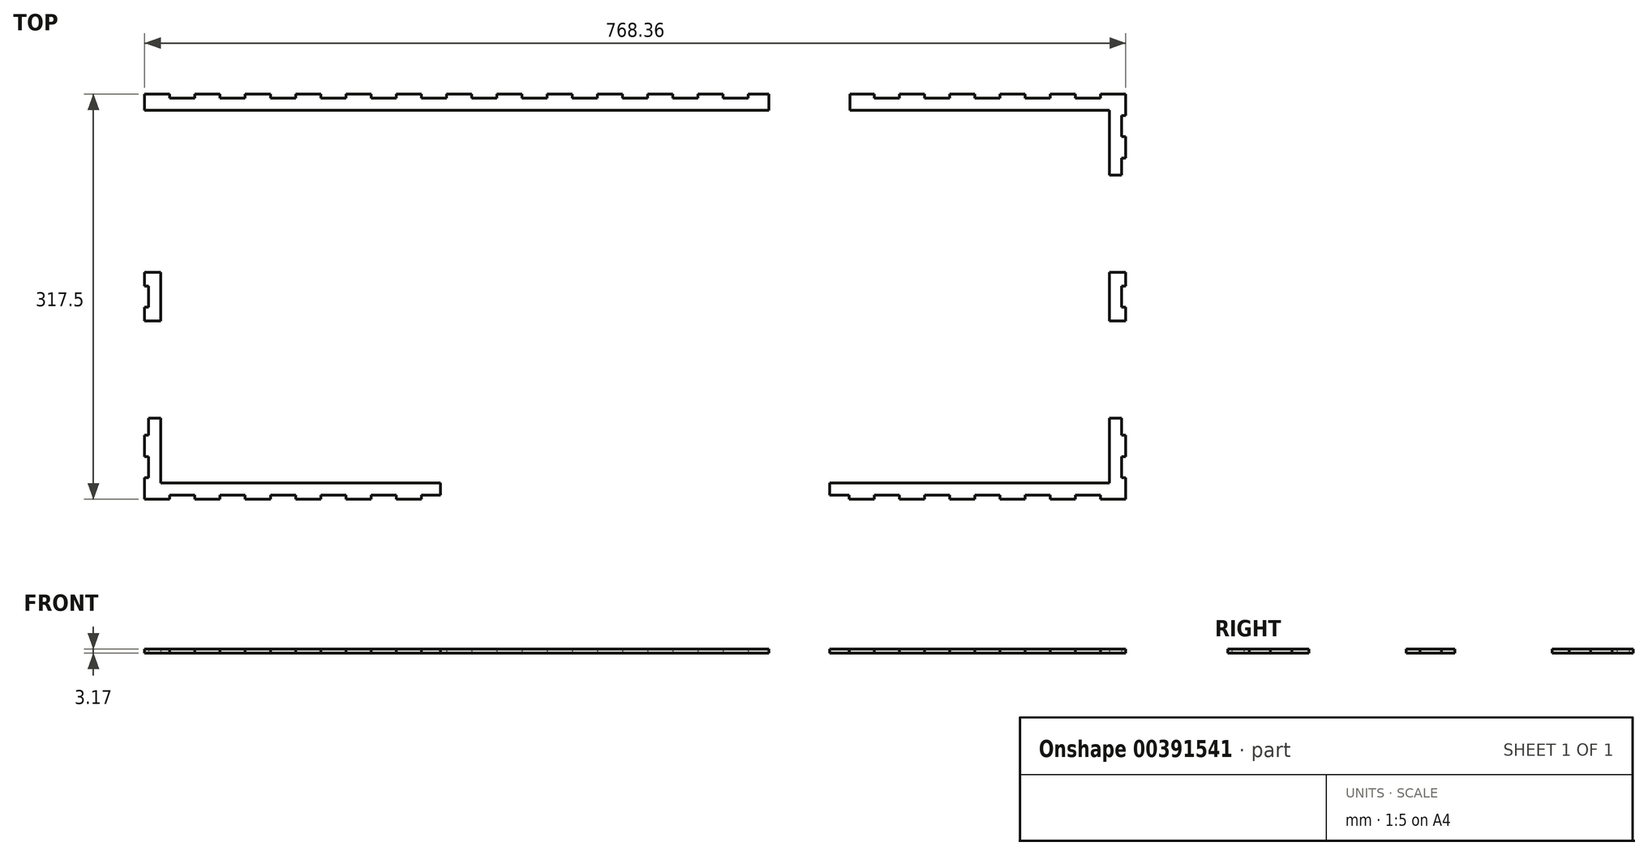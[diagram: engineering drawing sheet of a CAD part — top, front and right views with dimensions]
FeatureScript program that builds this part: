
annotation { "Feature Type Name" : "Feature", "Feature Type Description" : "" }
export const myFeature = defineFeature(function(context is Context, id is Id, definition is map)
    precondition{}
    {
        {
            var Q0;
            Q0=qCreatedBy(makeId("Top.planeOp"),FACE);
            var sketch = newSketch(context, id + "F0", { "sketchPlane" : qUnion([Q0])});
            skLineSegment(sketch, "E0.right", {"start": v(-384.18, -158.75) * mm, "end": v(-384.18, 158.75) * mm, "construction": true});
            skPoint(sketch, "E0.middle", {"position": v(0, 0) * mm});
            skLineSegment(sketch, "E1.bottom", {"start": v(-384.18, 158.75) * mm, "end": v(-364.47, 158.75) * mm});
            skLineSegment(sketch, "E1.left", {"start": v(-384.18, 158.75) * mm, "end": v(-384.18, 142.04) * mm});
            skLineSegment(sketch, "E2.right", {"start": v(-381, 142.04) * mm, "end": v(-381, 125.33) * mm});
            skLineSegment(sketch, "E3", {"start": v(-384.18, 142.04) * mm, "end": v(-381, 142.04) * mm});
            skLineSegment(sketch, "E4", {"start": v(-364.47, 158.75) * mm, "end": v(-364.47, 155.57) * mm});
            skLineSegment(sketch, "E5", {"start": v(-364.47, 155.57) * mm, "end": v(-344.77, 155.57) * mm});
            skLineSegment(sketch, "E6", {"start": v(384.18, 158.75) * mm, "end": v(-384.18, 158.75) * mm, "construction": true});
            skLineSegment(sketch, "E7", {"start": v(-381, 125.33) * mm, "end": v(-384.18, 125.33) * mm});
            skLineSegment(sketch, "E8.1.0.1", {"start": v(-384.18, 108.62) * mm, "end": v(-381, 108.62) * mm});
            skLineSegment(sketch, "E8.1.0.3", {"start": v(-384.17, 125.33) * mm, "end": v(-384.18, 108.62) * mm});
            skLineSegment(sketch, "E8.4.0.0", {"start": v(-381, -8.36) * mm, "end": v(-384.17, -8.36) * mm});
            skLineSegment(sketch, "E8.4.0.1", {"start": v(-384.17, 8.36) * mm, "end": v(-381, 8.36) * mm});
            skLineSegment(sketch, "E8.4.0.2", {"start": v(-381, 8.36) * mm, "end": v(-381, -8.36) * mm});
            skLineSegment(sketch, "E8.7.0.0", {"start": v(-381, -108.62) * mm, "end": v(-384.17, -108.62) * mm});
            skLineSegment(sketch, "E8.8.0.0", {"start": v(-381, -142.04) * mm, "end": v(-384.17, -142.04) * mm});
            skLineSegment(sketch, "E8.8.0.1", {"start": v(-384.17, -125.33) * mm, "end": v(-381, -125.33) * mm});
            skLineSegment(sketch, "E8.8.0.2", {"start": v(-381, -125.33) * mm, "end": v(-381, -142.04) * mm});
            skLineSegment(sketch, "E8.8.0.3", {"start": v(-384.17, -108.62) * mm, "end": v(-384.17, -125.33) * mm});
            skLineSegment(sketch, "E8.9.0.1", {"start": v(-384.17, -158.75) * mm, "end": v(-381, -158.75) * mm});
            skLineSegment(sketch, "E8.9.0.3", {"start": v(-384.17, -142.04) * mm, "end": v(-384.17, -158.75) * mm});
            skLineSegment(sketch, "E8.direction1", {"start": v(-384.18, 125.33) * mm, "end": v(-384.18, 91.9) * mm, "construction": true});
            skLineSegment(sketch, "E9", {"start": v(-344.77, 155.57) * mm, "end": v(-344.77, 158.75) * mm});
            skLineSegment(sketch, "E10.1.0.0", {"start": v(-325.07, 158.75) * mm, "end": v(-325.07, 155.58) * mm});
            skLineSegment(sketch, "E10.1.0.1", {"start": v(-325.07, 155.58) * mm, "end": v(-305.37, 155.58) * mm});
            skLineSegment(sketch, "E10.1.0.2", {"start": v(-305.37, 155.58) * mm, "end": v(-305.37, 158.75) * mm});
            skLineSegment(sketch, "E10.1.0.3", {"start": v(-344.77, 158.75) * mm, "end": v(-325.07, 158.75) * mm});
            skLineSegment(sketch, "E10.2.0.0", {"start": v(-285.67, 158.75) * mm, "end": v(-285.67, 155.58) * mm});
            skLineSegment(sketch, "E10.2.0.1", {"start": v(-285.67, 155.58) * mm, "end": v(-265.97, 155.58) * mm});
            skLineSegment(sketch, "E10.2.0.2", {"start": v(-265.97, 155.58) * mm, "end": v(-265.97, 158.75) * mm});
            skLineSegment(sketch, "E10.2.0.3", {"start": v(-305.37, 158.75) * mm, "end": v(-285.67, 158.75) * mm});
            skLineSegment(sketch, "E10.3.0.0", {"start": v(-246.27, 158.75) * mm, "end": v(-246.27, 155.58) * mm});
            skLineSegment(sketch, "E10.3.0.1", {"start": v(-246.27, 155.58) * mm, "end": v(-226.56, 155.58) * mm});
            skLineSegment(sketch, "E10.3.0.2", {"start": v(-226.56, 155.58) * mm, "end": v(-226.56, 158.75) * mm});
            skLineSegment(sketch, "E10.3.0.3", {"start": v(-265.97, 158.75) * mm, "end": v(-246.27, 158.75) * mm});
            skLineSegment(sketch, "E10.4.0.0", {"start": v(-206.86, 158.75) * mm, "end": v(-206.86, 155.58) * mm});
            skLineSegment(sketch, "E10.4.0.1", {"start": v(-206.86, 155.58) * mm, "end": v(-187.16, 155.58) * mm});
            skLineSegment(sketch, "E10.4.0.2", {"start": v(-187.16, 155.58) * mm, "end": v(-187.16, 158.75) * mm});
            skLineSegment(sketch, "E10.4.0.3", {"start": v(-226.56, 158.75) * mm, "end": v(-206.86, 158.75) * mm});
            skLineSegment(sketch, "E10.5.0.0", {"start": v(-167.46, 158.75) * mm, "end": v(-167.46, 155.58) * mm});
            skLineSegment(sketch, "E10.5.0.1", {"start": v(-167.46, 155.58) * mm, "end": v(-147.76, 155.58) * mm});
            skLineSegment(sketch, "E10.5.0.2", {"start": v(-147.76, 155.58) * mm, "end": v(-147.76, 158.75) * mm});
            skLineSegment(sketch, "E10.5.0.3", {"start": v(-187.16, 158.75) * mm, "end": v(-167.46, 158.75) * mm});
            skLineSegment(sketch, "E10.6.0.0", {"start": v(-128.06, 158.75) * mm, "end": v(-128.06, 155.58) * mm});
            skLineSegment(sketch, "E10.6.0.1", {"start": v(-128.06, 155.58) * mm, "end": v(-108.36, 155.58) * mm});
            skLineSegment(sketch, "E10.6.0.2", {"start": v(-108.36, 155.58) * mm, "end": v(-108.36, 158.75) * mm});
            skLineSegment(sketch, "E10.6.0.3", {"start": v(-147.76, 158.75) * mm, "end": v(-128.06, 158.75) * mm});
            skLineSegment(sketch, "E10.7.0.0", {"start": v(-88.66, 158.75) * mm, "end": v(-88.66, 155.58) * mm});
            skLineSegment(sketch, "E10.7.0.1", {"start": v(-88.66, 155.58) * mm, "end": v(-68.95, 155.58) * mm});
            skLineSegment(sketch, "E10.7.0.2", {"start": v(-68.95, 155.58) * mm, "end": v(-68.95, 158.75) * mm});
            skLineSegment(sketch, "E10.7.0.3", {"start": v(-108.36, 158.75) * mm, "end": v(-88.66, 158.75) * mm});
            skLineSegment(sketch, "E10.8.0.0", {"start": v(-49.25, 158.75) * mm, "end": v(-49.25, 155.58) * mm});
            skLineSegment(sketch, "E10.8.0.1", {"start": v(-49.25, 155.58) * mm, "end": v(-29.55, 155.58) * mm});
            skLineSegment(sketch, "E10.8.0.2", {"start": v(-29.55, 155.58) * mm, "end": v(-29.55, 158.75) * mm});
            skLineSegment(sketch, "E10.8.0.3", {"start": v(-68.95, 158.75) * mm, "end": v(-49.25, 158.75) * mm});
            skLineSegment(sketch, "E10.9.0.0", {"start": v(-9.85, 158.75) * mm, "end": v(-9.85, 155.58) * mm});
            skLineSegment(sketch, "E10.9.0.1", {"start": v(-9.85, 155.58) * mm, "end": v(9.85, 155.58) * mm});
            skLineSegment(sketch, "E10.9.0.2", {"start": v(9.85, 155.58) * mm, "end": v(9.85, 158.75) * mm});
            skLineSegment(sketch, "E10.9.0.3", {"start": v(-29.55, 158.75) * mm, "end": v(-9.85, 158.75) * mm});
            skLineSegment(sketch, "E10.10.0.0", {"start": v(29.55, 158.75) * mm, "end": v(29.55, 155.58) * mm});
            skLineSegment(sketch, "E10.10.0.1", {"start": v(29.55, 155.58) * mm, "end": v(49.25, 155.58) * mm});
            skLineSegment(sketch, "E10.10.0.2", {"start": v(49.25, 155.58) * mm, "end": v(49.25, 158.75) * mm});
            skLineSegment(sketch, "E10.10.0.3", {"start": v(9.85, 158.75) * mm, "end": v(29.55, 158.75) * mm});
            skLineSegment(sketch, "E10.11.0.0", {"start": v(68.95, 158.75) * mm, "end": v(68.95, 155.58) * mm});
            skLineSegment(sketch, "E10.11.0.1", {"start": v(68.95, 155.58) * mm, "end": v(88.66, 155.58) * mm});
            skLineSegment(sketch, "E10.11.0.2", {"start": v(88.66, 155.58) * mm, "end": v(88.66, 158.75) * mm});
            skLineSegment(sketch, "E10.11.0.3", {"start": v(49.25, 158.75) * mm, "end": v(68.95, 158.75) * mm});
            skLineSegment(sketch, "E10.12.0.0", {"start": v(108.36, 158.75) * mm, "end": v(108.36, 155.58) * mm});
            skLineSegment(sketch, "E10.12.0.3", {"start": v(88.66, 158.75) * mm, "end": v(108.36, 158.75) * mm});
            skLineSegment(sketch, "E10.16.0.2", {"start": v(285.67, 155.58) * mm, "end": v(285.67, 158.75) * mm});
            skLineSegment(sketch, "E10.17.0.0", {"start": v(305.37, 158.75) * mm, "end": v(305.37, 155.58) * mm});
            skLineSegment(sketch, "E10.17.0.1", {"start": v(305.37, 155.58) * mm, "end": v(325.07, 155.58) * mm});
            skLineSegment(sketch, "E10.17.0.2", {"start": v(325.07, 155.58) * mm, "end": v(325.07, 158.75) * mm});
            skLineSegment(sketch, "E10.17.0.3", {"start": v(285.67, 158.75) * mm, "end": v(305.37, 158.75) * mm});
            skLineSegment(sketch, "E10.18.0.0", {"start": v(344.77, 158.75) * mm, "end": v(344.77, 155.58) * mm});
            skLineSegment(sketch, "E10.18.0.1", {"start": v(344.77, 155.58) * mm, "end": v(364.47, 155.58) * mm});
            skLineSegment(sketch, "E10.18.0.2", {"start": v(364.47, 155.58) * mm, "end": v(364.47, 158.75) * mm});
            skLineSegment(sketch, "E10.18.0.3", {"start": v(325.07, 158.75) * mm, "end": v(344.77, 158.75) * mm});
            skLineSegment(sketch, "E10.19.0.0", {"start": v(384.18, 158.75) * mm, "end": v(384.18, 155.58) * mm});
            skLineSegment(sketch, "E10.19.0.3", {"start": v(364.47, 158.75) * mm, "end": v(384.18, 158.75) * mm});
            skLineSegment(sketch, "E10.direction1", {"start": v(-384.18, 158.75) * mm, "end": v(-344.77, 158.75) * mm, "construction": true});
            skLineSegment(sketch, "E11.MirrorCS", {"start": v(384.18, -158.75) * mm, "end": v(384.18, -155.58) * mm});
            skLineSegment(sketch, "E12.MirrorCS", {"start": v(-344.77, -155.57) * mm, "end": v(-344.77, -158.75) * mm});
            skLineSegment(sketch, "E13.MirrorCS", {"start": v(108.36, -158.75) * mm, "end": v(108.36, -155.58) * mm});
            skLineSegment(sketch, "E14.MirrorCS", {"start": v(285.67, -155.58) * mm, "end": v(285.67, -158.75) * mm});
            skLineSegment(sketch, "E15.MirrorCS", {"start": v(-285.67, -158.75) * mm, "end": v(-285.67, -155.58) * mm});
            skLineSegment(sketch, "E16.MirrorCS", {"start": v(49.25, -155.58) * mm, "end": v(49.25, -158.75) * mm});
            skLineSegment(sketch, "E17.MirrorCS", {"start": v(-108.36, -155.58) * mm, "end": v(-108.36, -158.75) * mm});
            skLineSegment(sketch, "E18.MirrorCS", {"start": v(-265.97, -155.58) * mm, "end": v(-265.97, -158.75) * mm});
            skLineSegment(sketch, "E19.MirrorCS", {"start": v(-29.55, -155.58) * mm, "end": v(-29.55, -158.75) * mm});
            skLineSegment(sketch, "E20.MirrorCS", {"start": v(364.47, -155.58) * mm, "end": v(364.47, -158.75) * mm});
            skLineSegment(sketch, "E21.MirrorCS", {"start": v(-206.86, -158.75) * mm, "end": v(-206.86, -155.58) * mm});
            skLineSegment(sketch, "E22.MirrorCS", {"start": v(-147.76, -155.58) * mm, "end": v(-147.76, -158.75) * mm});
            skLineSegment(sketch, "E23.MirrorCS", {"start": v(-305.37, -155.58) * mm, "end": v(-305.37, -158.75) * mm});
            skLineSegment(sketch, "E24.MirrorCS", {"start": v(206.86, -155.58) * mm, "end": v(206.86, -158.75) * mm});
            skLineSegment(sketch, "E25.MirrorCS", {"start": v(344.77, -158.75) * mm, "end": v(344.77, -155.58) * mm});
            skLineSegment(sketch, "E26.MirrorCS", {"start": v(128.06, -155.58) * mm, "end": v(128.06, -158.75) * mm});
            skLineSegment(sketch, "E27.MirrorCS", {"start": v(9.85, -155.58) * mm, "end": v(9.85, -158.75) * mm});
            skLineSegment(sketch, "E28.MirrorCS", {"start": v(-364.47, -158.75) * mm, "end": v(-364.47, -155.57) * mm});
            skLineSegment(sketch, "E29.MirrorCS", {"start": v(325.07, -155.58) * mm, "end": v(325.07, -158.75) * mm});
            skLineSegment(sketch, "E30.MirrorCS", {"start": v(167.46, -155.58) * mm, "end": v(167.46, -158.75) * mm});
            skLineSegment(sketch, "E31.MirrorCS", {"start": v(147.76, -158.75) * mm, "end": v(147.76, -155.58) * mm});
            skLineSegment(sketch, "E32.MirrorCS", {"start": v(305.37, -158.75) * mm, "end": v(305.37, -155.58) * mm});
            skLineSegment(sketch, "E33.MirrorCS", {"start": v(-88.66, -158.75) * mm, "end": v(-88.66, -155.58) * mm});
            skLineSegment(sketch, "E34.MirrorCS", {"start": v(29.55, -158.75) * mm, "end": v(29.55, -155.58) * mm});
            skLineSegment(sketch, "E35.MirrorCS", {"start": v(-128.06, -158.75) * mm, "end": v(-128.06, -155.58) * mm});
            skLineSegment(sketch, "E36.MirrorCS", {"start": v(-226.56, -155.58) * mm, "end": v(-226.56, -158.75) * mm});
            skLineSegment(sketch, "E37.MirrorCS", {"start": v(88.66, -155.58) * mm, "end": v(88.66, -158.75) * mm});
            skLineSegment(sketch, "E38.MirrorCS", {"start": v(246.27, -155.58) * mm, "end": v(246.27, -158.75) * mm});
            skLineSegment(sketch, "E39.MirrorCS", {"start": v(-68.95, -155.58) * mm, "end": v(-68.95, -158.75) * mm});
            skLineSegment(sketch, "E40.MirrorCS", {"start": v(265.97, -158.75) * mm, "end": v(265.97, -155.58) * mm});
            skLineSegment(sketch, "E41.MirrorCS", {"start": v(-325.07, -158.75) * mm, "end": v(-325.07, -155.58) * mm});
            skLineSegment(sketch, "E42.MirrorCS", {"start": v(187.16, -158.75) * mm, "end": v(187.16, -155.58) * mm});
            skLineSegment(sketch, "E43.MirrorCS", {"start": v(-187.16, -155.58) * mm, "end": v(-187.16, -158.75) * mm});
            skLineSegment(sketch, "E44.MirrorCS", {"start": v(-167.46, -158.75) * mm, "end": v(-167.46, -155.58) * mm});
            skLineSegment(sketch, "E45.MirrorCS", {"start": v(-9.85, -158.75) * mm, "end": v(-9.85, -155.58) * mm});
            skLineSegment(sketch, "E46.MirrorCS", {"start": v(-246.27, -158.75) * mm, "end": v(-246.27, -155.58) * mm});
            skLineSegment(sketch, "E47.MirrorCS", {"start": v(226.56, -158.75) * mm, "end": v(226.56, -155.58) * mm});
            skLineSegment(sketch, "E48.MirrorCS", {"start": v(68.95, -158.75) * mm, "end": v(68.95, -155.58) * mm});
            skLineSegment(sketch, "E49.MirrorCS", {"start": v(-49.25, -158.75) * mm, "end": v(-49.25, -155.58) * mm});
            skLineSegment(sketch, "E50.MirrorCS", {"start": v(-68.95, -158.75) * mm, "end": v(-49.25, -158.75) * mm});
            skLineSegment(sketch, "E51.MirrorCS", {"start": v(-226.56, -158.75) * mm, "end": v(-206.86, -158.75) * mm});
            skLineSegment(sketch, "E52.MirrorCS", {"start": v(246.27, -158.75) * mm, "end": v(265.97, -158.75) * mm});
            skLineSegment(sketch, "E53.MirrorCS", {"start": v(206.86, -158.75) * mm, "end": v(226.56, -158.75) * mm});
            skLineSegment(sketch, "E54.MirrorCS", {"start": v(49.25, -158.75) * mm, "end": v(68.95, -158.75) * mm});
            skLineSegment(sketch, "E55.MirrorCS", {"start": v(-265.97, -158.75) * mm, "end": v(-246.27, -158.75) * mm});
            skLineSegment(sketch, "E56.MirrorCS", {"start": v(-108.36, -158.75) * mm, "end": v(-88.66, -158.75) * mm});
            skLineSegment(sketch, "E57.MirrorCS", {"start": v(88.66, -158.75) * mm, "end": v(108.36, -158.75) * mm});
            skLineSegment(sketch, "E58.MirrorCS", {"start": v(-344.77, -158.75) * mm, "end": v(-325.07, -158.75) * mm});
            skLineSegment(sketch, "E59.MirrorCS", {"start": v(285.67, -158.75) * mm, "end": v(305.37, -158.75) * mm});
            skLineSegment(sketch, "E60.MirrorCS", {"start": v(128.06, -158.75) * mm, "end": v(147.76, -158.75) * mm});
            skLineSegment(sketch, "E61.MirrorCS", {"start": v(-384.18, -158.75) * mm, "end": v(-364.47, -158.75) * mm});
            skLineSegment(sketch, "E62.MirrorCS", {"start": v(167.46, -158.75) * mm, "end": v(187.16, -158.75) * mm});
            skLineSegment(sketch, "E63.MirrorCS", {"start": v(325.07, -158.75) * mm, "end": v(344.77, -158.75) * mm});
            skLineSegment(sketch, "E64.MirrorCS", {"start": v(364.47, -158.75) * mm, "end": v(384.18, -158.75) * mm});
            skLineSegment(sketch, "E65.MirrorCS", {"start": v(-29.55, -158.75) * mm, "end": v(-9.85, -158.75) * mm});
            skLineSegment(sketch, "E66.MirrorCS", {"start": v(-187.16, -158.75) * mm, "end": v(-167.46, -158.75) * mm});
            skLineSegment(sketch, "E67.MirrorCS", {"start": v(-305.37, -158.75) * mm, "end": v(-285.67, -158.75) * mm});
            skLineSegment(sketch, "E68.MirrorCS", {"start": v(-147.76, -158.75) * mm, "end": v(-128.06, -158.75) * mm});
            skLineSegment(sketch, "E69.MirrorCS", {"start": v(9.85, -158.75) * mm, "end": v(29.55, -158.75) * mm});
            skLineSegment(sketch, "E70.MirrorCS", {"start": v(29.55, -155.58) * mm, "end": v(49.25, -155.58) * mm});
            skLineSegment(sketch, "E71.MirrorCS", {"start": v(226.56, -155.58) * mm, "end": v(246.27, -155.58) * mm});
            skLineSegment(sketch, "E72.MirrorCS", {"start": v(-88.66, -155.58) * mm, "end": v(-68.95, -155.58) * mm});
            skLineSegment(sketch, "E73.MirrorCS", {"start": v(-49.25, -155.58) * mm, "end": v(-29.55, -155.58) * mm});
            skLineSegment(sketch, "E74.MirrorCS", {"start": v(-206.86, -155.58) * mm, "end": v(-187.16, -155.58) * mm});
            skLineSegment(sketch, "E75.MirrorCS", {"start": v(-364.47, -155.57) * mm, "end": v(-344.77, -155.57) * mm});
            skLineSegment(sketch, "E76.MirrorCS", {"start": v(384.18, -158.75) * mm, "end": v(-384.18, -158.75) * mm, "construction": true});
            skLineSegment(sketch, "E77.MirrorCS", {"start": v(-128.06, -155.58) * mm, "end": v(-108.36, -155.58) * mm});
            skLineSegment(sketch, "E78.MirrorCS", {"start": v(-285.67, -155.58) * mm, "end": v(-265.97, -155.58) * mm});
            skLineSegment(sketch, "E79.MirrorCS", {"start": v(344.77, -155.58) * mm, "end": v(364.47, -155.58) * mm});
            skLineSegment(sketch, "E80.MirrorCS", {"start": v(-9.85, -155.58) * mm, "end": v(9.85, -155.58) * mm});
            skLineSegment(sketch, "E81.MirrorCS", {"start": v(-167.46, -155.58) * mm, "end": v(-147.76, -155.58) * mm});
            skLineSegment(sketch, "E82.MirrorCS", {"start": v(-325.07, -155.58) * mm, "end": v(-305.37, -155.58) * mm});
            skLineSegment(sketch, "E83.MirrorCS", {"start": v(305.37, -155.58) * mm, "end": v(325.07, -155.58) * mm});
            skLineSegment(sketch, "E84.MirrorCS", {"start": v(147.76, -155.58) * mm, "end": v(167.46, -155.58) * mm});
            skLineSegment(sketch, "E85.MirrorCS", {"start": v(265.97, -155.58) * mm, "end": v(285.67, -155.58) * mm});
            skLineSegment(sketch, "E86.MirrorCS", {"start": v(-246.27, -155.58) * mm, "end": v(-226.56, -155.58) * mm});
            skLineSegment(sketch, "E87.MirrorCS", {"start": v(68.95, -155.58) * mm, "end": v(88.66, -155.58) * mm});
            skLineSegment(sketch, "E88.MirrorCS", {"start": v(187.16, -155.58) * mm, "end": v(206.86, -155.58) * mm});
            skLineSegment(sketch, "E89.MirrorCS", {"start": v(-384.18, -158.75) * mm, "end": v(-344.77, -158.75) * mm, "construction": true});
            skLineSegment(sketch, "E90.MirrorCS", {"start": v(108.36, -155.58) * mm, "end": v(128.06, -155.58) * mm});
            skLineSegment(sketch, "E91.MirrorCS", {"start": v(384.17, -158.75) * mm, "end": v(381, -158.75) * mm});
            skLineSegment(sketch, "E92.MirrorCS", {"start": v(384.18, 108.62) * mm, "end": v(381, 108.62) * mm});
            skLineSegment(sketch, "E93.MirrorCS", {"start": v(381, 125.33) * mm, "end": v(384.18, 125.33) * mm});
            skLineSegment(sketch, "E94.MirrorCS", {"start": v(381, -108.62) * mm, "end": v(384.17, -108.62) * mm});
            skLineSegment(sketch, "E95.MirrorCS", {"start": v(384.18, 142.04) * mm, "end": v(381, 142.04) * mm});
            skLineSegment(sketch, "E96.MirrorCS", {"start": v(381, -142.04) * mm, "end": v(384.17, -142.04) * mm});
            skLineSegment(sketch, "E97.MirrorCS", {"start": v(384.17, 8.36) * mm, "end": v(381, 8.36) * mm});
            skLineSegment(sketch, "E98.MirrorCS", {"start": v(384.17, -125.33) * mm, "end": v(381, -125.33) * mm});
            skLineSegment(sketch, "E99.MirrorCS", {"start": v(384.17, 125.33) * mm, "end": v(384.18, 108.62) * mm});
            skLineSegment(sketch, "E100.MirrorCS", {"start": v(381, -8.36) * mm, "end": v(384.17, -8.36) * mm});
            skLineSegment(sketch, "E101.MirrorCS", {"start": v(384.17, -142.04) * mm, "end": v(384.17, -158.75) * mm});
            skLineSegment(sketch, "E102.MirrorCS", {"start": v(384.18, 158.75) * mm, "end": v(384.18, 142.04) * mm});
            skLineSegment(sketch, "E103.MirrorCS", {"start": v(384.17, -108.62) * mm, "end": v(384.17, -125.33) * mm});
            skLineSegment(sketch, "E104.MirrorCS", {"start": v(381, 142.04) * mm, "end": v(381, 125.33) * mm});
            skLineSegment(sketch, "E105.MirrorCS", {"start": v(381, 8.36) * mm, "end": v(381, -8.36) * mm});
            skLineSegment(sketch, "E106.MirrorCS", {"start": v(384.18, -158.75) * mm, "end": v(384.18, 158.75) * mm, "construction": true});
            skLineSegment(sketch, "E107.MirrorCS", {"start": v(381, -125.33) * mm, "end": v(381, -142.04) * mm});
            skLineSegment(sketch, "E108.bottom", {"start": v(371.48, -146.05) * mm, "end": v(-371.48, -146.05) * mm});
            skLineSegment(sketch, "E108.top", {"start": v(371.48, 146.05) * mm, "end": v(-371.48, 146.05) * mm});
            skLineSegment(sketch, "E108.left", {"start": v(371.48, -146.05) * mm, "end": v(371.48, 146.05) * mm});
            skLineSegment(sketch, "E108.right", {"start": v(-371.48, -146.05) * mm, "end": v(-371.48, 146.05) * mm});
            skLineSegment(sketch, "E109", {"start": v(353.63, -95.25) * mm, "end": v(314.49, -95.25) * mm, "construction": true});
            skLineSegment(sketch, "E110", {"start": v(314.51, -19.05) * mm, "end": v(356.15, -19.05) * mm, "construction": true});
            skLineSegment(sketch, "E111", {"start": v(317.24, 19.05) * mm, "end": v(357.03, 19.05) * mm, "construction": true});
            skLineSegment(sketch, "E112", {"start": v(317.78, 95.25) * mm, "end": v(359.55, 95.25) * mm, "construction": true});
            skLineSegment(sketch, "E113", {"start": v(381, -108.62) * mm, "end": v(381, -95.25) * mm});
            skLineSegment(sketch, "E114", {"start": v(384.18, -8.36) * mm, "end": v(384.18, -19.05) * mm});
            skLineSegment(sketch, "E115", {"start": v(381, -95.25) * mm, "end": v(371.48, -95.25) * mm});
            skLineSegment(sketch, "E116", {"start": v(384.18, -19.05) * mm, "end": v(371.48, -19.05) * mm});
            skLineSegment(sketch, "E117", {"start": v(384.17, 8.36) * mm, "end": v(384.18, 19.05) * mm});
            skLineSegment(sketch, "E118", {"start": v(381, 108.62) * mm, "end": v(381, 95.25) * mm});
            skLineSegment(sketch, "E119", {"start": v(384.18, 19.05) * mm, "end": v(371.48, 19.05) * mm});
            skLineSegment(sketch, "E120", {"start": v(381, 95.25) * mm, "end": v(371.48, 95.25) * mm});
            skLineSegment(sketch, "E121.MirrorCS", {"start": v(-314.51, -19.05) * mm, "end": v(-356.15, -19.05) * mm, "construction": true});
            skLineSegment(sketch, "E122.MirrorCS", {"start": v(-317.78, 95.25) * mm, "end": v(-359.55, 95.25) * mm, "construction": true});
            skLineSegment(sketch, "E123.MirrorCS", {"start": v(-353.63, -95.25) * mm, "end": v(-314.49, -95.25) * mm, "construction": true});
            skLineSegment(sketch, "E124.MirrorCS", {"start": v(-317.24, 19.05) * mm, "end": v(-357.03, 19.05) * mm, "construction": true});
            skLineSegment(sketch, "E125", {"start": v(-381, -108.62) * mm, "end": v(-381, -95.25) * mm});
            skLineSegment(sketch, "E126", {"start": v(-381, -95.25) * mm, "end": v(-371.48, -95.25) * mm});
            skLineSegment(sketch, "E127", {"start": v(-381, 108.62) * mm, "end": v(-381, 95.25) * mm});
            skLineSegment(sketch, "E128", {"start": v(-381, 95.25) * mm, "end": v(-371.48, 95.25) * mm});
            skLineSegment(sketch, "E129", {"start": v(-384.18, -8.36) * mm, "end": v(-384.18, -19.05) * mm});
            skLineSegment(sketch, "E130", {"start": v(-384.18, -19.05) * mm, "end": v(-371.48, -19.05) * mm});
            skLineSegment(sketch, "E131", {"start": v(104.78, 110.81) * mm, "end": v(104.78, 136.48) * mm, "construction": true});
            skLineSegment(sketch, "E132", {"start": v(168.28, 138.21) * mm, "end": v(168.28, 115.73) * mm, "construction": true});
            skLineSegment(sketch, "E133", {"start": v(108.36, 155.58) * mm, "end": v(111.13, 155.58) * mm});
            skLineSegment(sketch, "E134", {"start": v(285.67, 155.58) * mm, "end": v(268.6, 155.58) * mm});
            skLineSegment(sketch, "E135", {"start": v(-384.18, 19.05) * mm, "end": v(-384.17, 8.36) * mm});
            skLineSegment(sketch, "E136", {"start": v(-384.18, 19.05) * mm, "end": v(-371.48, 19.05) * mm});
            skLineSegment(sketch, "E137.MirrorCS", {"start": v(167.46, 155.58) * mm, "end": v(167.46, 158.75) * mm});
            skLineSegment(sketch, "E138.MirrorCS", {"start": v(147.76, 158.75) * mm, "end": v(147.76, 155.58) * mm});
            skLineSegment(sketch, "E139.MirrorCS", {"start": v(128.06, 155.58) * mm, "end": v(128.06, 158.75) * mm});
            skLineSegment(sketch, "E140.MirrorCS", {"start": v(265.97, 158.75) * mm, "end": v(265.97, 155.58) * mm});
            skLineSegment(sketch, "E141.MirrorCS", {"start": v(246.27, 155.58) * mm, "end": v(246.27, 158.75) * mm});
            skLineSegment(sketch, "E142.MirrorCS", {"start": v(226.56, 158.75) * mm, "end": v(226.56, 155.58) * mm});
            skLineSegment(sketch, "E143.MirrorCS", {"start": v(187.16, 158.75) * mm, "end": v(187.16, 155.58) * mm});
            skLineSegment(sketch, "E144.MirrorCS", {"start": v(206.86, 155.58) * mm, "end": v(206.86, 158.75) * mm});
            skLineSegment(sketch, "E145.MirrorCS", {"start": v(265.97, 155.58) * mm, "end": v(285.67, 155.58) * mm});
            skLineSegment(sketch, "E146.MirrorCS", {"start": v(206.86, 158.75) * mm, "end": v(226.56, 158.75) * mm});
            skLineSegment(sketch, "E147.MirrorCS", {"start": v(147.76, 155.58) * mm, "end": v(167.46, 155.58) * mm});
            skLineSegment(sketch, "E148.MirrorCS", {"start": v(246.27, 158.75) * mm, "end": v(265.97, 158.75) * mm});
            skLineSegment(sketch, "E149.MirrorCS", {"start": v(167.46, 158.75) * mm, "end": v(187.16, 158.75) * mm});
            skLineSegment(sketch, "E150.MirrorCS", {"start": v(128.06, 158.75) * mm, "end": v(147.76, 158.75) * mm});
            skLineSegment(sketch, "E151.MirrorCS", {"start": v(108.36, 155.58) * mm, "end": v(128.06, 155.58) * mm});
            skLineSegment(sketch, "E152.MirrorCS", {"start": v(187.16, 155.58) * mm, "end": v(206.86, 155.58) * mm});
            skLineSegment(sketch, "E153.MirrorCS", {"start": v(226.56, 155.58) * mm, "end": v(246.27, 155.58) * mm});
            skLineSegment(sketch, "E154", {"start": v(168.28, 138.21) * mm, "end": v(168.28, 188.5) * mm, "construction": true});
            skLineSegment(sketch, "E155.bottom", {"start": v(104.78, 110.81) * mm, "end": v(168.28, 110.81) * mm});
            skLineSegment(sketch, "E155.top", {"start": v(104.78, 188.5) * mm, "end": v(168.28, 188.5) * mm});
            skLineSegment(sketch, "E155.left", {"start": v(104.78, 110.81) * mm, "end": v(104.77, 188.5) * mm});
            skLineSegment(sketch, "E155.right", {"start": v(168.28, 110.81) * mm, "end": v(168.28, 188.5) * mm});
            skLineSegment(sketch, "E156", {"start": v(-436.86, 146.05) * mm, "end": v(-309.02, 146.05) * mm, "construction": true});
            skLineSegment(sketch, "E157.bottom", {"start": v(-436.86, 146.05) * mm, "end": v(-317.78, 146.05) * mm});
            skLineSegment(sketch, "E157.top", {"start": v(-436.86, 95.25) * mm, "end": v(-317.78, 95.25) * mm});
            skLineSegment(sketch, "E157.left", {"start": v(-436.86, 146.05) * mm, "end": v(-436.86, 95.25) * mm});
            skLineSegment(sketch, "E157.right", {"start": v(-317.78, 146.05) * mm, "end": v(-317.78, 95.25) * mm});
            skLineSegment(sketch, "E158", {"start": v(-152.4, -11.84) * mm, "end": v(-152.4, -292.06) * mm, "construction": true});
            skLineSegment(sketch, "E159", {"start": v(152.4, -4.45) * mm, "end": v(152.4, -285.28) * mm, "construction": true});
            skLineSegment(sketch, "E160", {"start": v(-152.4, -146.05) * mm, "end": v(-152.4, -155.58) * mm});
            skLineSegment(sketch, "E161", {"start": v(152.4, -146.05) * mm, "end": v(152.4, -155.58) * mm});
            skSolve(sketch);
        }
        {
            var Q0;
            Q0=makeQuery(id+"F0.imprint","IMPRINT",FACE,{"disambiguationData":[TD([[makeQuery(id+"F0.imprint","IMPRINT",EDGE,{"derivedFrom":sQuery(id+"F0.wireOp",EDGE,"E10.17.0.0")}),-1.0]])]});
            var Q1;
            Q1=makeQuery(id+"F0.imprint","IMPRINT",FACE,{"disambiguationData":[TD([[makeQuery(id+"F0.imprint","IMPRINT",EDGE,{"derivedFrom":sQuery(id+"F0.wireOp",EDGE,"E1.bottom")}),-1.0]])]});
            var Q2;
            Q2=makeQuery(id+"F0.imprint","IMPRINT",FACE,{"disambiguationData":[TD([[makeQuery(id+"F0.imprint","IMPRINT",EDGE,{"derivedFrom":sQuery(id+"F0.wireOp",EDGE,"E8.4.0.0")}),1.0]])]});
            var Q3;
            Q3=makeQuery(id+"F0.imprint","IMPRINT",FACE,{"disambiguationData":[TD([[makeQuery(id+"F0.imprint","IMPRINT",EDGE,{"derivedFrom":sQuery(id+"F0.wireOp",EDGE,"E8.7.0.0")}),1.0]])]});
            var Q4;
            Q4=makeQuery(id+"F0.imprint","IMPRINT",FACE,{"disambiguationData":[TD([[makeQuery(id+"F0.imprint","IMPRINT",EDGE,{"derivedFrom":sQuery(id+"F0.wireOp",EDGE,"E97.MirrorCS")}),-1.0]])]});
            var Q5;
            Q5=makeQuery(id+"F0.imprint","IMPRINT",FACE,{"disambiguationData":[TD([[makeQuery(id+"F0.imprint","IMPRINT",EDGE,{"derivedFrom":sQuery(id+"F0.wireOp",EDGE,"E14.MirrorCS")}),1.0]])]});
            extrude(context, id + "F1", {"entities" : qUnion([Q0, Q1, Q2, Q3, Q4, Q5]), "depth" : 3.17 * mm});
        }
    });
